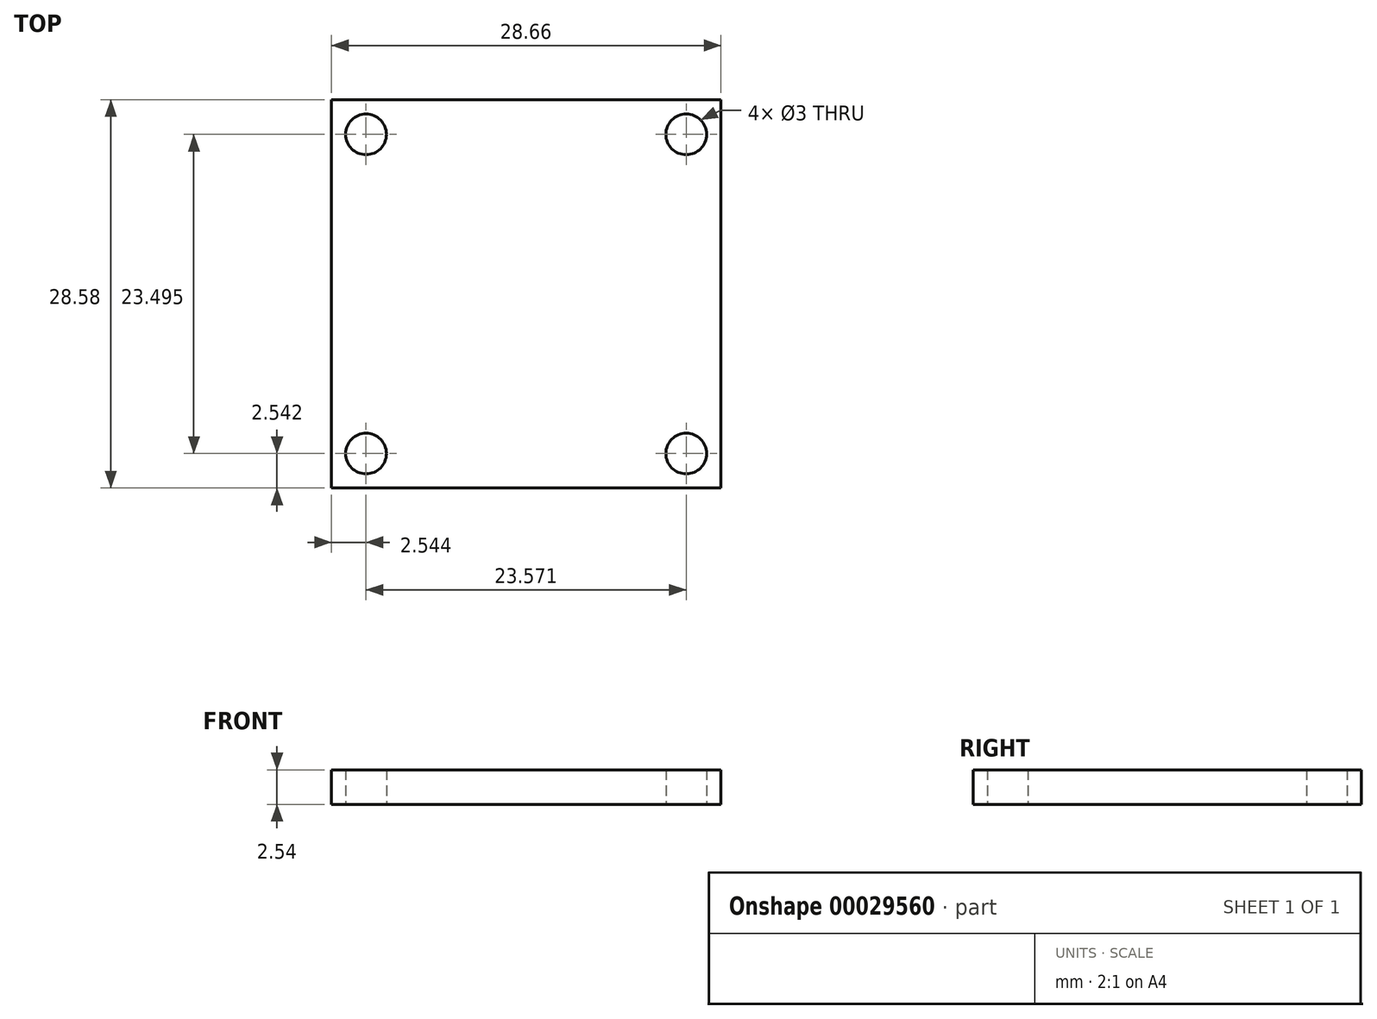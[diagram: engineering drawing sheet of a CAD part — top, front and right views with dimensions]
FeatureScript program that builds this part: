
annotation { "Feature Type Name" : "Feature", "Feature Type Description" : "" }
export const myFeature = defineFeature(function(context is Context, id is Id, definition is map)
    precondition{}
    {
        {
            var Q0;
            Q0=qCreatedBy(makeId("Top.planeOp"),FACE);
            var sketch = newSketch(context, id + "F0", { "sketchPlane" : qUnion([Q0])});
            skLineSegment(sketch, "E0.rect.bottom", {"start": v(14.33, 14.29) * mm, "end": v(-14.33, 14.29) * mm});
            skLineSegment(sketch, "E0.rect.top", {"start": v(14.33, -14.29) * mm, "end": v(-14.33, -14.29) * mm});
            skLineSegment(sketch, "E0.rect.left", {"start": v(14.33, 14.29) * mm, "end": v(14.33, -14.29) * mm});
            skLineSegment(sketch, "E0.rect.right", {"start": v(-14.33, 14.29) * mm, "end": v(-14.33, -14.29) * mm});
            skPoint(sketch, "E0.rect.middle", {"position": v(0, 0) * mm});
            skCircle(sketch, "E1", {"center": v(-11.79, 11.75) * mm, "radius": 1.5 * mm});
            skCircle(sketch, "E2", {"center": v(-11.79, -11.75) * mm, "radius": 1.5 * mm});
            skCircle(sketch, "E3", {"center": v(11.79, 11.75) * mm, "radius": 1.5 * mm});
            skCircle(sketch, "E4", {"center": v(11.79, -11.75) * mm, "radius": 1.5 * mm});
            skSolve(sketch);
        }
        {
            var Q0;
            Q0 = qSketchRegion(id + "F0", true);
            extrude(context, id + "F1", {"entities" : qUnion([Q0]), "depth" : 2.54 * mm});
        }
    });
